# Revit family: NBS_Allermuir_DmstcChrs_Mote-en-us_Sofa120
name_source: partatom
category: Furniture
revit_build: Autodesk Revit 2016 (Build: 20151007_0715(x64)
units: mm (PartAtom-declared; Revit-internal decimal feet)

## family parameters
Always vertical = Yes
Cut with Voids When Loaded = No
Room Calculation Point = No
Shared = No
Work Plane-Based = No

## types (2) — shared parameters
AssetType = Moveable
Category = Pr_40_50_12_22:Dining chairs
DurationUnit = year
ExpectedLife = 10
FrameColourOptions = Flint grey, mineral sand, mellow yellow, orange crush
FrameHeight = 10 "
FrameMountingMaterial = NBS_Concept
FramesColour = Black
FramesFinish = Powder coat
FramesMaterial = Aluminum
IfcExportAs = IfcFurnitureType
IfcExportType = SOFA
IsBuiltIn = No
JoiningArmOffset = 1 "
ManufacturerName = Allermuir
ManufacturerURL = http://www.thesenatorgroup.com
NBSCertification = www.nationalbimlibrary.com/cert/gealcozu
NBSDescription = Domestic chairs
NBSReference = 45-35-20/365
NominalDepth = 80 "
NominalLength = 41 "
NominalWidth = 80 "
OmniClassCode = 22-12 52 23
OmniClassTitle = Office Seating
OmniClassVersion = Table 22 2012-05-16
ProductInformation = http://www.thesenatorgroup.com
ScreenFinishMaterial = NBS_Concept
ScreenHeight = 41 "
SeatAngle = 120.00°
SeatArmRestHeight = 24 "
SeatEndRestOffset = 3 "
SeatFrameMaterial = NBS_Concept
SeatFrameWidth = 2 "
SeatLegOffset = 6 "
SeatOverallWidth = 80 "
SeatPowerSupplyMaterial = NBS_Concept
SeatScreenHeight = 52 "
SeatingArmRestMaterial = NBS_Concept
SeatingHeight = 19 "
SeatingSeatMaterial = NBS_Concept
SeatsAndBacksFinish = Two-tone upholstery
SeatsAndBacksMaterial = Upholstered
Status = UNSET
Uniclass2015Code = Pr_40_50_12_22
Uniclass2015Title = Dining chairs
Uniclass2015Version = Products v1.9
Version = 1
WarrantyDescription = Allermuir warrant that its manufactured products are free from manufacturing defects in materials or workmanship for a period of ten years
WarrantyDurationParts = 10
WarrantyDurationUnit = year
zero-valued in all types: HighestSeatingHeight, LowestSeatingHeight

## per-type parameters (varying)
| type | BIMObjectName | Description | Features | HasScreen | ModelReference | Name | NominalHeight | OptionalAccessories | Size |
| MTESF120 | NBS_Allermuir_DomesticChairs_Mote_MTESF120-US | 120° sofa | Fully upholstered, cast aluminum legs and aluminum perimeter frame finished in black powder coat, plastic glides with leveling adjustment, two-tone upholstery, 1 x front facing, frame integrated power unit - 2 x powered USB and 1 x power outlet, 2 x rear facing, frame integrated power unit - 2 x powered USB and 1 x power outlet | No | Mote sofa | DomesticChairs_Mote_MTE-SF120_Allermuir | 33 " | 1 x front facing frame intergrated power unit with 2 x powered USB and 1 x power socket, 2 x rear facing frame intergrated power unit with 2 x powered USB and 1 x power socket | 40.5 x 80.25 x 32.75" |
| MTEBSS120 | NBS_Allermuir_DomesticChairs_Mote_MTEBSS120-US | 120° angled sofa with rear screen | Rear screens, fully upholstered, cast aluminium legs and aluminium perimeter frame finished in black powder coat, plastic glides with leveling adjustment, two-tone upholstery | Yes | Mote with rear screen | DomesticChairs_Mote_MTE-BSS120-US_Allermuir | 51 " | 1 x front facing frame intergrated power unit 2 x powered USB and 1 x power socket, 2 x rear facing frame intergrated power unit 2 x powered USB and 1 x power socket | 40.5 x 80.25 x 51" |

note: column(s) folded — value = type name in every type: ModelNumber

## geometry (parser evidence)
native form markers: Sweep x7
no freeform markers — native parametric forms only
